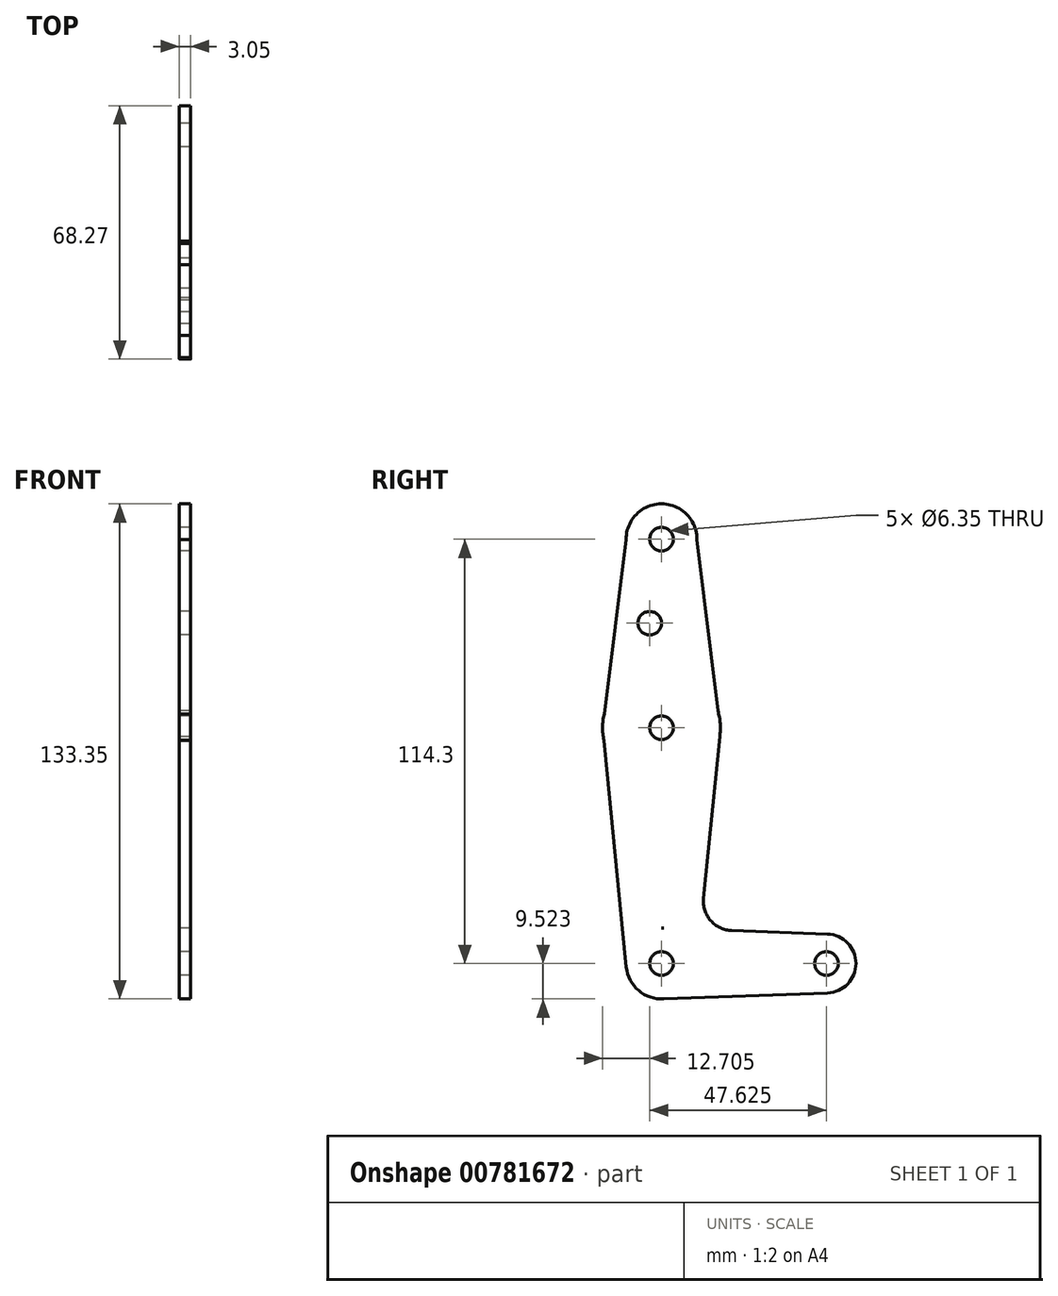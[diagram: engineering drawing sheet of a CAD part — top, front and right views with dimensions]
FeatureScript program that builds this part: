
annotation { "Feature Type Name" : "Feature", "Feature Type Description" : "" }
export const myFeature = defineFeature(function(context is Context, id is Id, definition is map)
    precondition{}
    {
        {
            var Q0;
            Q0=qCreatedBy(makeId("Right.planeOp"),FACE);
            var sketch = newSketch(context, id + "F0", { "sketchPlane" : qUnion([Q0])});
            skLineSegment(sketch, "E0", {"start": v(0, -55.14) * mm, "end": v(44.45, -55.14) * mm});
            skCircle(sketch, "E1", {"center": v(44.45, -55.14) * mm, "radius": 7.94 * mm});
            skCircle(sketch, "E2", {"center": v(0, 8.36) * mm, "radius": 15.88 * mm});
            skCircle(sketch, "E3", {"center": v(0, 59.16) * mm, "radius": 9.53 * mm});
            skLineSegment(sketch, "E4", {"start": v(0, -55.14) * mm, "end": v(0, 59.16) * mm, "construction": true});
            skLineSegment(sketch, "E5", {"start": v(-9.52, 59.04) * mm, "end": v(-15.87, 8.6) * mm});
            skLineSegment(sketch, "E6", {"start": v(9.52, 59.04) * mm, "end": v(15.86, 7.58) * mm});
            skCircle(sketch, "E7", {"center": v(0, -55.14) * mm, "radius": 9.53 * mm});
            skLineSegment(sketch, "E8", {"start": v(15.86, 7.58) * mm, "end": v(11.33, -37.55) * mm});
            skLineSegment(sketch, "E9", {"start": v(-15.87, 8.6) * mm, "end": v(-9.48, -56.07) * mm});
            skLineSegment(sketch, "E10", {"start": v(0, -45.61) * mm, "end": v(0.68, -45.64) * mm});
            skLineSegment(sketch, "E11", {"start": v(0, -64.66) * mm, "end": v(44.73, -63.07) * mm});
            skCircle(sketch, "E12", {"center": v(0, 59.16) * mm, "radius": 3.17 * mm});
            skCircle(sketch, "E13", {"center": v(0, 8.36) * mm, "radius": 3.18 * mm});
            skCircle(sketch, "E14", {"center": v(0, -55.14) * mm, "radius": 3.17 * mm});
            skCircle(sketch, "E15", {"center": v(44.45, -55.14) * mm, "radius": 3.18 * mm});
            skCircle(sketch, "E16", {"center": v(-3.18, 36.53) * mm, "radius": 3.18 * mm});
            skLineSegment(sketch, "E17.trimOffspring", {"start": v(18.96, -46.29) * mm, "end": v(44.73, -47.2) * mm});
            skPoint(sketch, "E18.visualSharp", {"position": v(10.49, -45.99) * mm});
            skArc(sketch, "E18.filletArc", {"start": v(11.33, -37.55) * mm, "mid": v(13.26, -43.57) * mm, "end": v(18.96, -46.29) * mm});
            skSolve(sketch);
        }
        {
            var Q0;
            Q0 = qSketchRegion(id + "F0", true);
            extrude(context, id + "F1", {"entities" : qUnion([Q0]), "depth" : 3.05 * mm, "offsetDistance" : 25.4 * mm});
        }
    });
